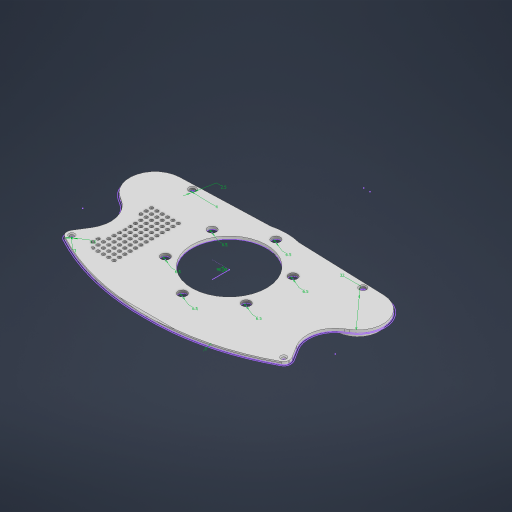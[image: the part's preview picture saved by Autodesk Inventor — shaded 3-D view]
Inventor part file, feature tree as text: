
AUTODESK INVENTOR PART (.ipt)
format: ipt  version: 2023 (Build 270158000, 158)  size: 451,072 bytes
history: native  units: mm
features: sketch x6, extrude x6, projected_geometry x3, chamfer x1, pattern_linear x1, split x1
ambient origin geometry x8: Origin, YZ Plane, XZ Plane, XY Plane, X Axis, Y Axis, Z Axis, Center Point
bodies: Solid1 (feature_tree)
feature tree (18):
  sketch  "Sketch1"  dims[d0=1.5mm d1=2.5mm d3=3.0mm d4=4.0mm d6=1.0mm d7=90.0deg d8=2.0mm d9=0.0mm d10=0.75mm d11=2.0mm d12=45.0deg]
  extrude  "Extrusion1"  Depth=2.0mm TaperAngle=0.0deg
  chamfer  "Chamfer1"  Distance=2.0mm Angle=45.0deg
  extrude  "Extrusion2"  Depth=4.0mm
  pattern_linear  "Rectangular Pattern1"  Count1=13 Spacing1=4.0mm
  extrude  "Extrusion3"  Depth=6.0mm
  extrude  "Extrusion4"  Depth=4.5mm
  split  "Split1"
  extrude  "Extrusion6"  TaperAngle=45.0deg  [1 undecoded]
  extrude  "Extrusion7"  Depth=4.5mm TaperAngle=0.0deg
  sketch  "Sketch2"  dims[d15=2.5mm d16=4.0mm]
  sketch  "Sketch3"  dims[d17=4.0mm]
  sketch  "Sketch4"  dims[d18=0.0mm d19=0.0mm d20=130.0mm d22=4.0mm d23=60.0mm d25=4.0mm]
  sketch  "Sketch5"  dims[d26=10.0mm d27=6.0mm]
  projected_geometry  "Projected Loop1"
  projected_geometry  "Projected Loop2"
  sketch  "Sketch7"  dims[d28=10.0mm d29=0.0mm d31=1.0mm d32=45.0deg d33=100.0mm d34=0.0mm d37=5.0mm d38=0.0mm d39=6.5mm d40=6.5mm d41=6.5mm d42=6.5mm d43=6.5mm d45=6.5mm d46=32.0mm d47=4.5mm d48=0.0mm]
  projected_geometry  "Projected Loop5"
note: 1 required parameter value undecoded (feature->parameter linkage not recoverable at this tier; creation-order binding heuristic only, values carry confidence <= 0.55)
